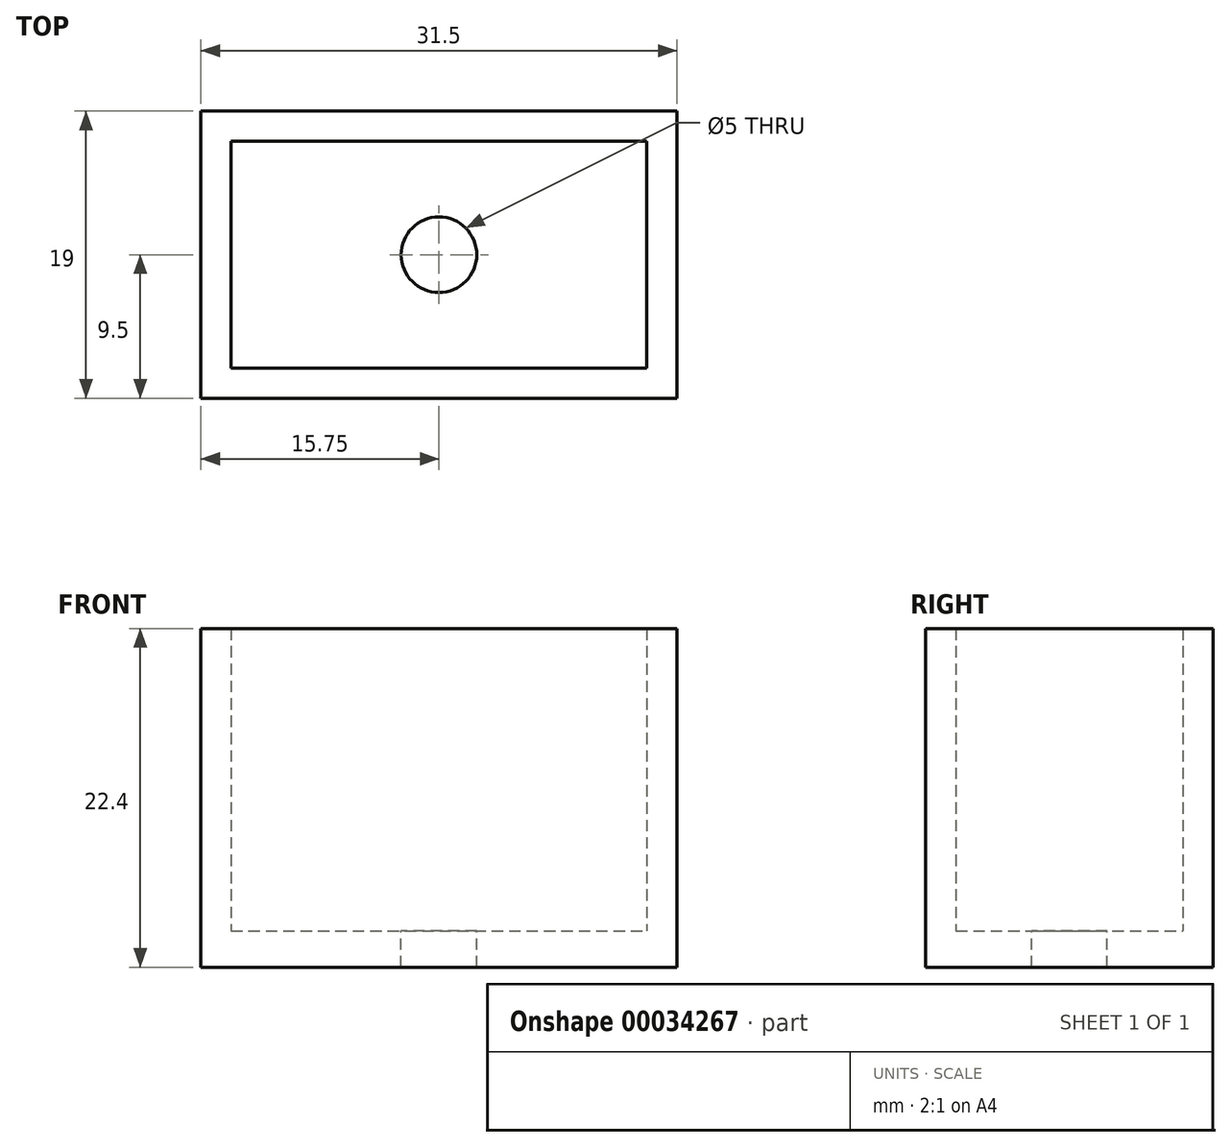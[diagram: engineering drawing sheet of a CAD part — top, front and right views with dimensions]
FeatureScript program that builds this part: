
annotation { "Feature Type Name" : "Feature", "Feature Type Description" : "" }
export const myFeature = defineFeature(function(context is Context, id is Id, definition is map)
    precondition{}
    {
        {
            var Q0;
            Q0=qCreatedBy(makeId("Top.planeOp"),FACE);
            var sketch = newSketch(context, id + "F0", { "sketchPlane" : qUnion([Q0])});
            skLineSegment(sketch, "E0.bottom", {"start": v(0, 0) * mm, "end": v(27.5, 0) * mm});
            skLineSegment(sketch, "E0.top", {"start": v(0, 15) * mm, "end": v(27.5, 15) * mm});
            skLineSegment(sketch, "E0.left", {"start": v(0, 0) * mm, "end": v(0, 15) * mm});
            skLineSegment(sketch, "E0.right", {"start": v(27.5, 0) * mm, "end": v(27.5, 15) * mm});
            skLineSegment(sketch, "E1.0", {"start": v(-2, 17) * mm, "end": v(29.5, 17) * mm});
            skLineSegment(sketch, "E1.1", {"start": v(-2, -2) * mm, "end": v(-2, 17) * mm});
            skLineSegment(sketch, "E1.2", {"start": v(-2, -2) * mm, "end": v(29.5, -2) * mm});
            skLineSegment(sketch, "E1.3", {"start": v(29.5, -2) * mm, "end": v(29.5, 17) * mm});
            skCircle(sketch, "E2", {"center": v(13.75, 7.5) * mm, "radius": 2.5 * mm});
            skSolve(sketch);
        }
        {
            var Q0;
            Q0=makeQuery(id+"F0.imprint","IMPRINT",FACE,{"disambiguationData":[TD([[makeQuery(id+"F0.imprint","IMPRINT",EDGE,{"derivedFrom":sQuery(id+"F0.wireOp",EDGE,"E0.bottom")}),-1.0]])]});
            extrude(context, id + "F1", {"entities" : qUnion([Q0]), "depth" : 20 * mm});
        }
        {
            var Q0;
            Q0=makeQuery(id+"F0.imprint","IMPRINT",FACE,{"disambiguationData":[TD([[makeQuery(id+"F0.imprint","IMPRINT",EDGE,{"derivedFrom":sQuery(id+"F0.wireOp",EDGE,"E0.bottom")}),1.0]])]});
            var Q1;
            Q1=makeQuery(id+"F0.imprint","IMPRINT",FACE,{"disambiguationData":[TD([[makeQuery(id+"F0.imprint","IMPRINT",EDGE,{"derivedFrom":sQuery(id+"F0.wireOp",EDGE,"E0.bottom")}),-1.0]])]});
            extrude(context, id + "F2", {"entities" : qUnion([Q0, Q1]), "operationType" : NewBodyOperationType.ADD, "oppositeDirection" : true, "depth" : 2.4 * mm});
        }
    });
